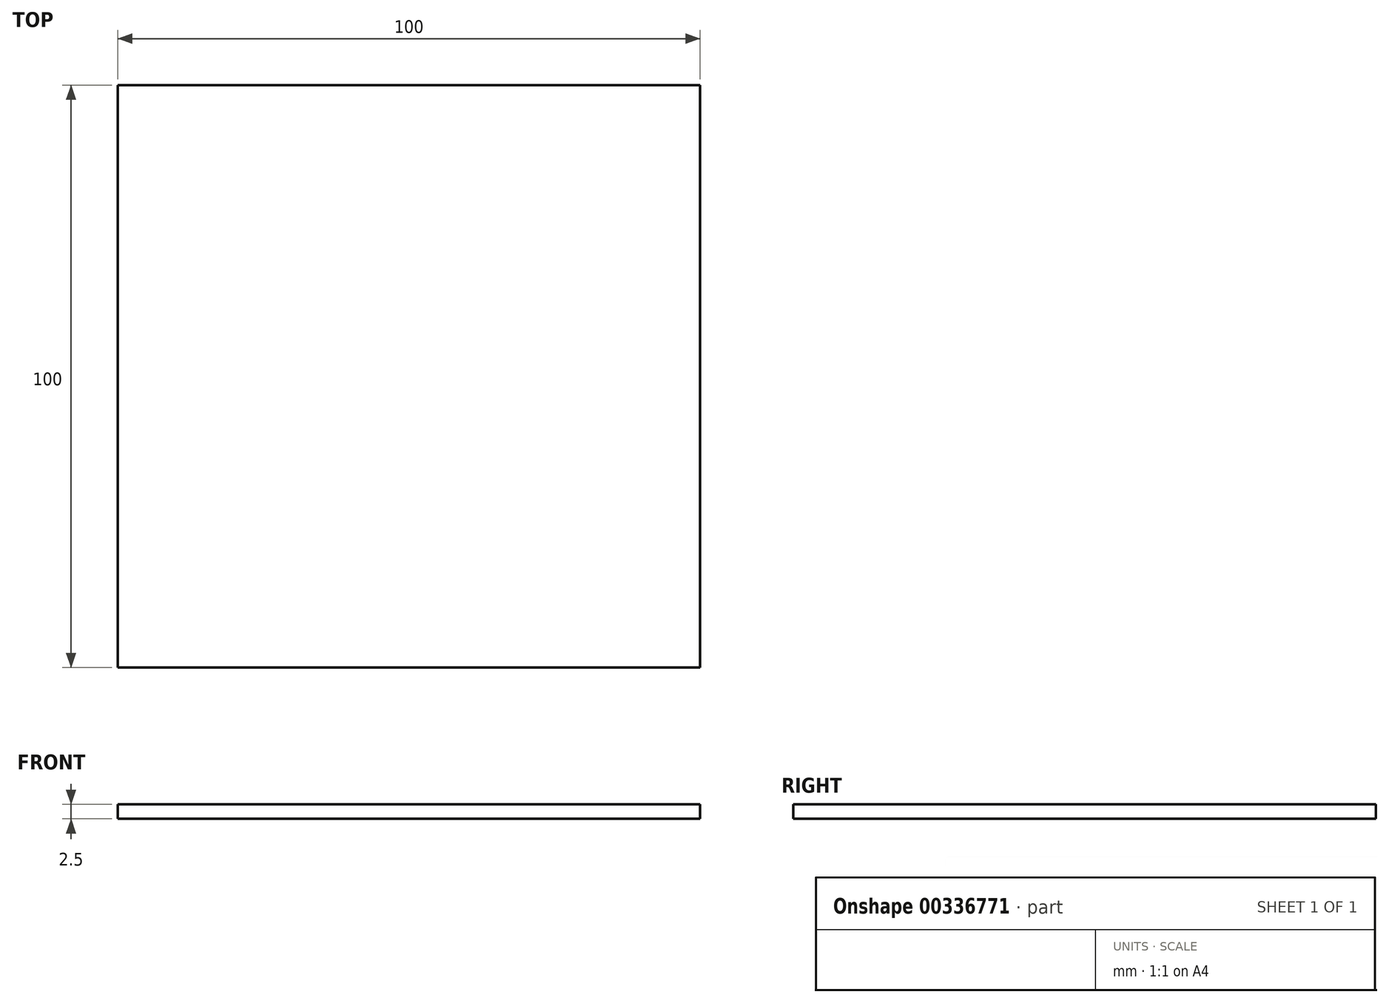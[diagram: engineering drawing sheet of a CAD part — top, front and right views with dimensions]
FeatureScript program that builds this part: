
annotation { "Feature Type Name" : "Feature", "Feature Type Description" : "" }
export const myFeature = defineFeature(function(context is Context, id is Id, definition is map)
    precondition{}
    {
        {
            var Q0;
            Q0=qCreatedBy(makeId("Top.planeOp"),FACE);
            var sketch = newSketch(context, id + "F0", { "sketchPlane" : qUnion([Q0])});
            skLineSegment(sketch, "E0.bottom", {"start": v(50, 50) * mm, "end": v(-50, 50) * mm});
            skLineSegment(sketch, "E0.top", {"start": v(50, -50) * mm, "end": v(-50, -50) * mm});
            skLineSegment(sketch, "E0.left", {"start": v(50, 50) * mm, "end": v(50, -50) * mm});
            skLineSegment(sketch, "E0.right", {"start": v(-50, 50) * mm, "end": v(-50, -50) * mm});
            skPoint(sketch, "E0.middle", {"position": v(0, 0) * mm});
            skSolve(sketch);
        }
        {
            var Q0;
            Q0=makeQuery(id+"F0.imprint","IMPRINT",FACE,{"disambiguationData":[TD([[makeQuery(id+"F0.imprint","IMPRINT",EDGE,{"derivedFrom":sQuery(id+"F0.wireOp",EDGE,"E0.bottom")}),1.0]])]});
            extrude(context, id + "F1", {"entities" : qUnion([Q0]), "depth" : 2.5 * mm});
        }
    });
